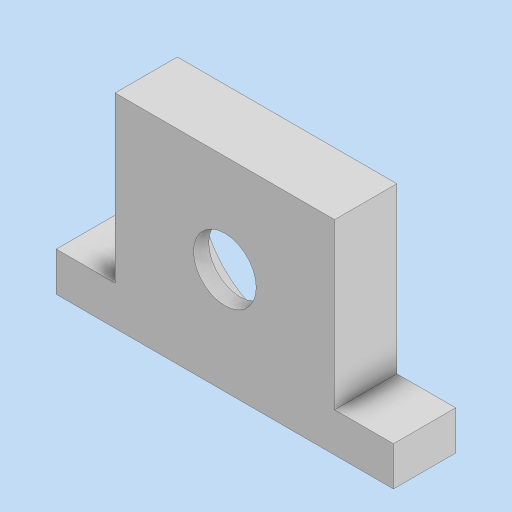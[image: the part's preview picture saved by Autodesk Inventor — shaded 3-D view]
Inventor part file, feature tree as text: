
AUTODESK INVENTOR PART (.ipt)
format: ipt  version: 2023 (Build 270158000, 158)  size: 119,808 bytes
history: native  units: mm
features: extrude x3, sketch x3
ambient origin geometry x8: Origin, YZ Plane, XZ Plane, XY Plane, X Axis, Y Axis, Z Axis, Center Point
bodies: Solid1 (feature_tree)
feature tree (6):
  extrude  "Extrusion1"  Depth=42.0mm
  extrude  "Extrusion2"  Depth=86.0mm
  extrude  "Extrusion3"  Depth=3.875mm
  sketch  "Sketch1"  dims[d4=52.0mm d5=42.0mm]
  sketch  "Sketch2"  dims[d6=56.0mm d7=86.0mm]
  sketch  "Sketch3"  dims[d8=10.0mm d9=27.0mm d10=45.0mm d11=15.875mm d12=0.0mm d13=3.875mm d14=0.0mm d15=16.0mm d16=3.875mm d17=0.0mm]
